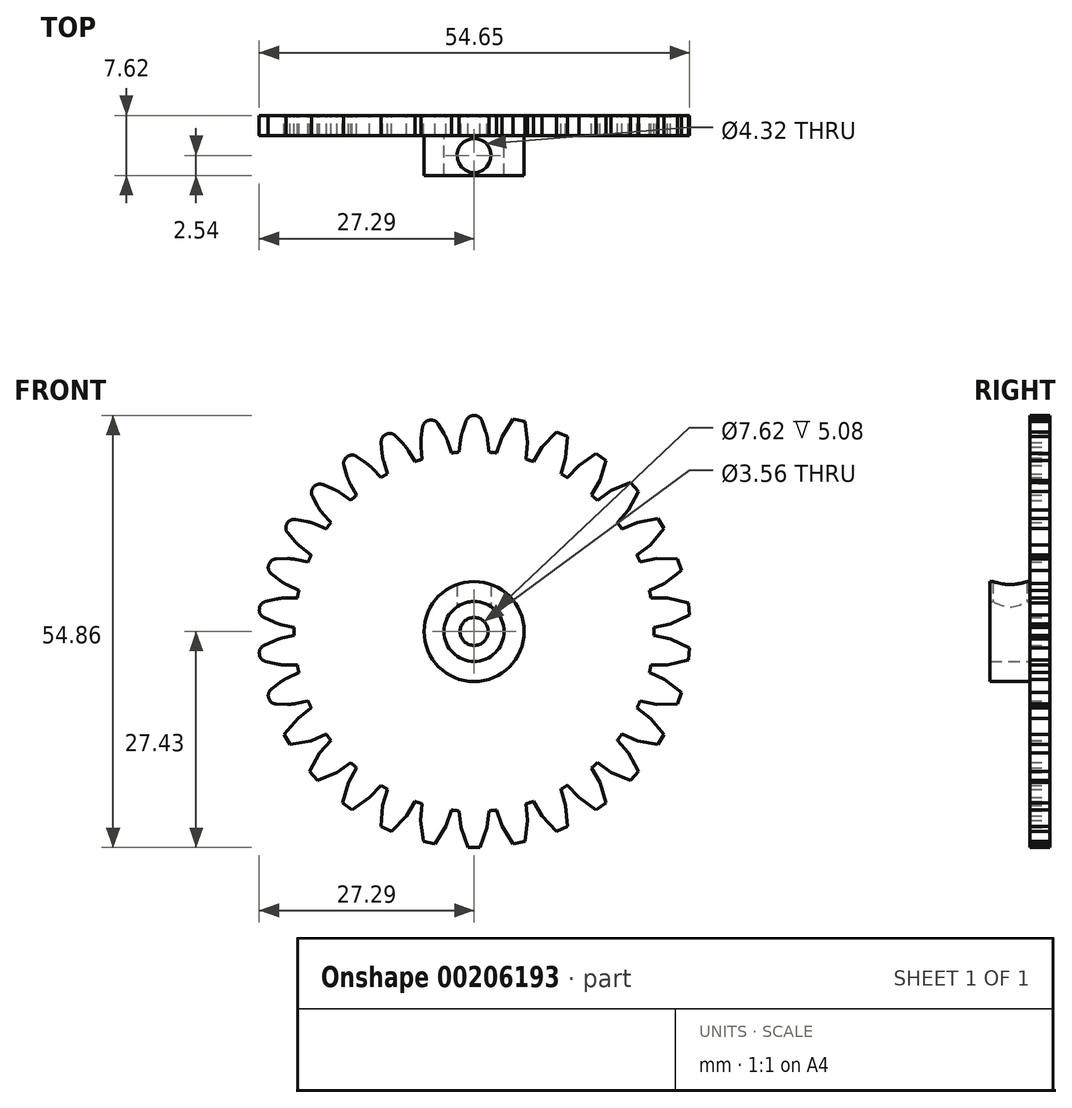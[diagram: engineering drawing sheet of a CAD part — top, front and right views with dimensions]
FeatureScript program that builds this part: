
annotation { "Feature Type Name" : "Feature", "Feature Type Description" : "" }
export const myFeature = defineFeature(function(context is Context, id is Id, definition is map)
    precondition{}
    {
        {
            var Q0;
            Q0=qCreatedBy(makeId("Front.planeOp"),FACE);
            var sketch = newSketch(context, id + "F0", { "sketchPlane" : qUnion([Q0])});
            skCircle(sketch, "E0", {"center": v(0, 0) * mm, "radius": 22.86 * mm});
            skLineSegment(sketch, "E1", {"start": v(-1.9, 22.78) * mm, "end": v(-0.76, 27.43) * mm, "construction": true});
            skLineSegment(sketch, "E2", {"start": v(-0.76, 27.43) * mm, "end": v(0.76, 27.43) * mm});
            skLineSegment(sketch, "E3", {"start": v(0.76, 27.43) * mm, "end": v(1.9, 22.78) * mm, "construction": true});
            skLineSegment(sketch, "E4", {"start": v(-1.9, 22.78) * mm, "end": v(-1.65, 24.9) * mm});
            skPoint(sketch, "E4.endSnap0", {"position": v(-1.33, 25.1) * mm});
            skLineSegment(sketch, "E5", {"start": v(-1.65, 24.9) * mm, "end": v(-0.76, 27.43) * mm});
            skLineSegment(sketch, "E6", {"start": v(1.9, 22.78) * mm, "end": v(1.65, 24.9) * mm});
            skPoint(sketch, "E6.endSnap0", {"position": v(1.33, 25.1) * mm});
            skLineSegment(sketch, "E7", {"start": v(1.65, 24.9) * mm, "end": v(0.76, 27.43) * mm});
            skLineSegment(sketch, "E8.1.0", {"start": v(-6.45, 26.67) * mm, "end": v(-4.96, 27) * mm});
            skLineSegment(sketch, "E8.1.1", {"start": v(-3.56, 24.7) * mm, "end": v(-4.96, 27) * mm});
            skLineSegment(sketch, "E8.1.2", {"start": v(-2.87, 22.68) * mm, "end": v(-3.56, 24.7) * mm});
            skLineSegment(sketch, "E8.1.3", {"start": v(-6.8, 24) * mm, "end": v(-6.45, 26.67) * mm});
            skLineSegment(sketch, "E8.1.4", {"start": v(-6.6, 21.89) * mm, "end": v(-6.8, 24) * mm});
            skLineSegment(sketch, "E8.2.0", {"start": v(-11.85, 24.75) * mm, "end": v(-10.46, 25.37) * mm});
            skLineSegment(sketch, "E8.2.1", {"start": v(-8.62, 23.41) * mm, "end": v(-10.46, 25.37) * mm});
            skLineSegment(sketch, "E8.2.2", {"start": v(-7.53, 21.59) * mm, "end": v(-8.62, 23.41) * mm});
            skLineSegment(sketch, "E8.2.3", {"start": v(-11.63, 22.07) * mm, "end": v(-11.85, 24.75) * mm});
            skLineSegment(sketch, "E8.2.4", {"start": v(-11, 20.04) * mm, "end": v(-11.63, 22.07) * mm});
            skLineSegment(sketch, "E8.3.0", {"start": v(-16.74, 21.75) * mm, "end": v(-15.5, 22.64) * mm});
            skLineSegment(sketch, "E8.3.1", {"start": v(-13.3, 21.1) * mm, "end": v(-15.5, 22.64) * mm});
            skLineSegment(sketch, "E8.3.2", {"start": v(-11.85, 19.55) * mm, "end": v(-13.3, 21.1) * mm});
            skLineSegment(sketch, "E8.3.3", {"start": v(-15.97, 19.17) * mm, "end": v(-16.74, 21.75) * mm});
            skLineSegment(sketch, "E8.3.4", {"start": v(-14.93, 17.31) * mm, "end": v(-15.97, 19.17) * mm});
            skLineSegment(sketch, "E8.4.0", {"start": v(-20.9, 17.79) * mm, "end": v(-19.88, 18.92) * mm});
            skLineSegment(sketch, "E8.4.1", {"start": v(-17.4, 17.88) * mm, "end": v(-19.88, 18.92) * mm});
            skLineSegment(sketch, "E8.4.2", {"start": v(-15.65, 16.66) * mm, "end": v(-17.4, 17.88) * mm});
            skLineSegment(sketch, "E8.4.3", {"start": v(-19.6, 15.43) * mm, "end": v(-20.9, 17.79) * mm});
            skLineSegment(sketch, "E8.4.4", {"start": v(-18.2, 13.83) * mm, "end": v(-19.6, 15.43) * mm});
            skLineSegment(sketch, "E8.5.0", {"start": v(-24.14, 13.06) * mm, "end": v(-23.38, 14.38) * mm});
            skLineSegment(sketch, "E8.5.1", {"start": v(-20.73, 13.88) * mm, "end": v(-23.38, 14.38) * mm});
            skLineSegment(sketch, "E8.5.2", {"start": v(-18.78, 13.04) * mm, "end": v(-20.73, 13.88) * mm});
            skLineSegment(sketch, "E8.5.3", {"start": v(-22.38, 11.02) * mm, "end": v(-24.14, 13.06) * mm});
            skLineSegment(sketch, "E8.5.4", {"start": v(-20.68, 9.74) * mm, "end": v(-22.38, 11.02) * mm});
            skLineSegment(sketch, "E8.6.0", {"start": v(-26.32, 7.75) * mm, "end": v(-25.85, 9.2) * mm});
            skLineSegment(sketch, "E8.6.1", {"start": v(-23.16, 9.26) * mm, "end": v(-25.85, 9.2) * mm});
            skLineSegment(sketch, "E8.6.2", {"start": v(-21.08, 8.85) * mm, "end": v(-23.16, 9.26) * mm});
            skLineSegment(sketch, "E8.6.3", {"start": v(-24.18, 6.12) * mm, "end": v(-26.32, 7.75) * mm});
            skLineSegment(sketch, "E8.6.4", {"start": v(-22.25, 5.23) * mm, "end": v(-24.18, 6.12) * mm});
            skLineSegment(sketch, "E8.7.0", {"start": v(-27.36, 2.1) * mm, "end": v(-27.2, 3.63) * mm});
            skLineSegment(sketch, "E8.7.1", {"start": v(-24.58, 4.24) * mm, "end": v(-27.2, 3.63) * mm});
            skLineSegment(sketch, "E8.7.2", {"start": v(-22.46, 4.28) * mm, "end": v(-24.58, 4.24) * mm});
            skLineSegment(sketch, "E8.7.3", {"start": v(-24.93, 0.96) * mm, "end": v(-27.36, 2.1) * mm});
            skLineSegment(sketch, "E8.7.4", {"start": v(-22.85, 0.49) * mm, "end": v(-24.93, 0.96) * mm});
            skLineSegment(sketch, "E8.8.0", {"start": v(-27.2, -3.63) * mm, "end": v(-27.36, -2.1) * mm});
            skLineSegment(sketch, "E8.8.1", {"start": v(-24.93, -0.96) * mm, "end": v(-27.36, -2.1) * mm});
            skLineSegment(sketch, "E8.8.2", {"start": v(-22.85, -0.49) * mm, "end": v(-24.93, -0.96) * mm});
            skLineSegment(sketch, "E8.8.3", {"start": v(-24.58, -4.24) * mm, "end": v(-27.2, -3.63) * mm});
            skLineSegment(sketch, "E8.8.4", {"start": v(-22.46, -4.28) * mm, "end": v(-24.58, -4.24) * mm});
            skLineSegment(sketch, "E8.9.0", {"start": v(-25.85, -9.2) * mm, "end": v(-26.32, -7.75) * mm});
            skLineSegment(sketch, "E8.9.1", {"start": v(-24.18, -6.12) * mm, "end": v(-26.32, -7.75) * mm});
            skLineSegment(sketch, "E8.9.2", {"start": v(-22.25, -5.23) * mm, "end": v(-24.18, -6.12) * mm});
            skLineSegment(sketch, "E8.9.3", {"start": v(-23.16, -9.26) * mm, "end": v(-25.85, -9.2) * mm});
            skLineSegment(sketch, "E8.9.4", {"start": v(-21.08, -8.85) * mm, "end": v(-23.16, -9.26) * mm});
            skCircle(sketch, "E9", {"center": v(0, 0) * mm, "radius": 1.78 * mm});
            skLineSegment(sketch, "E10.3.10.0", {"start": v(-22.38, -11.02) * mm, "end": v(-24.14, -13.06) * mm});
            skLineSegment(sketch, "E10.6.10.0", {"start": v(-20.68, -9.74) * mm, "end": v(-22.38, -11.02) * mm});
            skLineSegment(sketch, "E10.9.10.0", {"start": v(-20.73, -13.88) * mm, "end": v(-23.38, -14.38) * mm});
            skLineSegment(sketch, "E10.12.10.0", {"start": v(-18.78, -13.04) * mm, "end": v(-20.73, -13.88) * mm});
            skLineSegment(sketch, "E10.13.10.0", {"start": v(-23.38, -14.38) * mm, "end": v(-24.14, -13.06) * mm});
            skLineSegment(sketch, "E10.3.11.0", {"start": v(-19.6, -15.43) * mm, "end": v(-20.9, -17.79) * mm});
            skLineSegment(sketch, "E10.6.11.0", {"start": v(-18.2, -13.83) * mm, "end": v(-19.6, -15.43) * mm});
            skLineSegment(sketch, "E10.9.11.0", {"start": v(-17.4, -17.88) * mm, "end": v(-19.88, -18.92) * mm});
            skLineSegment(sketch, "E10.12.11.0", {"start": v(-15.65, -16.66) * mm, "end": v(-17.4, -17.88) * mm});
            skLineSegment(sketch, "E10.13.11.0", {"start": v(-19.88, -18.92) * mm, "end": v(-20.9, -17.79) * mm});
            skLineSegment(sketch, "E10.3.12.0", {"start": v(-15.97, -19.17) * mm, "end": v(-16.74, -21.75) * mm});
            skLineSegment(sketch, "E10.6.12.0", {"start": v(-14.93, -17.31) * mm, "end": v(-15.97, -19.17) * mm});
            skLineSegment(sketch, "E10.9.12.0", {"start": v(-13.3, -21.1) * mm, "end": v(-15.5, -22.64) * mm});
            skLineSegment(sketch, "E10.12.12.0", {"start": v(-11.85, -19.55) * mm, "end": v(-13.3, -21.1) * mm});
            skLineSegment(sketch, "E10.13.12.0", {"start": v(-15.5, -22.64) * mm, "end": v(-16.74, -21.75) * mm});
            skLineSegment(sketch, "E10.3.13.0", {"start": v(-11.63, -22.07) * mm, "end": v(-11.85, -24.75) * mm});
            skLineSegment(sketch, "E10.6.13.0", {"start": v(-11, -20.04) * mm, "end": v(-11.63, -22.07) * mm});
            skLineSegment(sketch, "E10.9.13.0", {"start": v(-8.62, -23.41) * mm, "end": v(-10.46, -25.37) * mm});
            skLineSegment(sketch, "E10.12.13.0", {"start": v(-7.53, -21.59) * mm, "end": v(-8.62, -23.41) * mm});
            skLineSegment(sketch, "E10.13.13.0", {"start": v(-10.46, -25.37) * mm, "end": v(-11.85, -24.75) * mm});
            skLineSegment(sketch, "E10.3.14.0", {"start": v(-6.8, -24) * mm, "end": v(-6.45, -26.67) * mm});
            skLineSegment(sketch, "E10.6.14.0", {"start": v(-6.6, -21.89) * mm, "end": v(-6.8, -24) * mm});
            skLineSegment(sketch, "E10.9.14.0", {"start": v(-3.56, -24.7) * mm, "end": v(-4.96, -27) * mm});
            skLineSegment(sketch, "E10.12.14.0", {"start": v(-2.87, -22.68) * mm, "end": v(-3.56, -24.7) * mm});
            skLineSegment(sketch, "E10.13.14.0", {"start": v(-4.96, -27) * mm, "end": v(-6.45, -26.67) * mm});
            skLineSegment(sketch, "E10.3.15.0", {"start": v(-1.65, -24.9) * mm, "end": v(-0.76, -27.43) * mm});
            skLineSegment(sketch, "E10.6.15.0", {"start": v(-1.9, -22.78) * mm, "end": v(-1.65, -24.9) * mm});
            skLineSegment(sketch, "E10.9.15.0", {"start": v(1.65, -24.9) * mm, "end": v(0.76, -27.43) * mm});
            skLineSegment(sketch, "E10.12.15.0", {"start": v(1.9, -22.78) * mm, "end": v(1.65, -24.9) * mm});
            skLineSegment(sketch, "E10.13.15.0", {"start": v(0.76, -27.43) * mm, "end": v(-0.76, -27.43) * mm});
            skLineSegment(sketch, "E10.3.16.0", {"start": v(3.56, -24.7) * mm, "end": v(4.96, -27) * mm});
            skLineSegment(sketch, "E10.6.16.0", {"start": v(2.87, -22.68) * mm, "end": v(3.56, -24.7) * mm});
            skLineSegment(sketch, "E10.9.16.0", {"start": v(6.8, -24) * mm, "end": v(6.45, -26.67) * mm});
            skLineSegment(sketch, "E10.12.16.0", {"start": v(6.6, -21.89) * mm, "end": v(6.8, -24) * mm});
            skLineSegment(sketch, "E10.13.16.0", {"start": v(6.45, -26.67) * mm, "end": v(4.96, -27) * mm});
            skLineSegment(sketch, "E10.3.17.0", {"start": v(8.62, -23.41) * mm, "end": v(10.46, -25.37) * mm});
            skLineSegment(sketch, "E10.6.17.0", {"start": v(7.53, -21.59) * mm, "end": v(8.62, -23.41) * mm});
            skLineSegment(sketch, "E10.9.17.0", {"start": v(11.63, -22.07) * mm, "end": v(11.85, -24.75) * mm});
            skLineSegment(sketch, "E10.12.17.0", {"start": v(11, -20.04) * mm, "end": v(11.63, -22.07) * mm});
            skLineSegment(sketch, "E10.13.17.0", {"start": v(11.85, -24.75) * mm, "end": v(10.46, -25.37) * mm});
            skLineSegment(sketch, "E10.3.18.0", {"start": v(13.3, -21.1) * mm, "end": v(15.5, -22.64) * mm});
            skLineSegment(sketch, "E10.6.18.0", {"start": v(11.85, -19.55) * mm, "end": v(13.3, -21.1) * mm});
            skLineSegment(sketch, "E10.9.18.0", {"start": v(15.97, -19.17) * mm, "end": v(16.74, -21.75) * mm});
            skLineSegment(sketch, "E10.12.18.0", {"start": v(14.93, -17.31) * mm, "end": v(15.97, -19.17) * mm});
            skLineSegment(sketch, "E10.13.18.0", {"start": v(16.74, -21.75) * mm, "end": v(15.5, -22.64) * mm});
            skLineSegment(sketch, "E10.3.19.0", {"start": v(17.4, -17.88) * mm, "end": v(19.88, -18.92) * mm});
            skLineSegment(sketch, "E10.6.19.0", {"start": v(15.65, -16.66) * mm, "end": v(17.4, -17.88) * mm});
            skLineSegment(sketch, "E10.9.19.0", {"start": v(19.6, -15.43) * mm, "end": v(20.9, -17.79) * mm});
            skLineSegment(sketch, "E10.12.19.0", {"start": v(18.2, -13.83) * mm, "end": v(19.6, -15.43) * mm});
            skLineSegment(sketch, "E10.13.19.0", {"start": v(20.9, -17.79) * mm, "end": v(19.88, -18.92) * mm});
            skLineSegment(sketch, "E11.3.20.0", {"start": v(20.73, -13.88) * mm, "end": v(23.38, -14.38) * mm});
            skLineSegment(sketch, "E11.6.20.0", {"start": v(18.78, -13.04) * mm, "end": v(20.73, -13.88) * mm});
            skLineSegment(sketch, "E11.9.20.0", {"start": v(22.38, -11.02) * mm, "end": v(24.14, -13.06) * mm});
            skLineSegment(sketch, "E11.12.20.0", {"start": v(20.68, -9.74) * mm, "end": v(22.38, -11.02) * mm});
            skLineSegment(sketch, "E11.13.20.0", {"start": v(24.14, -13.06) * mm, "end": v(23.38, -14.38) * mm});
            skLineSegment(sketch, "E11.3.21.0", {"start": v(23.16, -9.26) * mm, "end": v(25.85, -9.2) * mm});
            skLineSegment(sketch, "E11.6.21.0", {"start": v(21.08, -8.85) * mm, "end": v(23.16, -9.26) * mm});
            skLineSegment(sketch, "E11.9.21.0", {"start": v(24.18, -6.12) * mm, "end": v(26.32, -7.75) * mm});
            skLineSegment(sketch, "E11.12.21.0", {"start": v(22.25, -5.23) * mm, "end": v(24.18, -6.12) * mm});
            skLineSegment(sketch, "E11.13.21.0", {"start": v(26.32, -7.75) * mm, "end": v(25.85, -9.2) * mm});
            skLineSegment(sketch, "E11.3.22.0", {"start": v(24.58, -4.24) * mm, "end": v(27.2, -3.63) * mm});
            skLineSegment(sketch, "E11.6.22.0", {"start": v(22.46, -4.28) * mm, "end": v(24.58, -4.24) * mm});
            skLineSegment(sketch, "E11.9.22.0", {"start": v(24.93, -0.96) * mm, "end": v(27.36, -2.1) * mm});
            skLineSegment(sketch, "E11.12.22.0", {"start": v(22.85, -0.49) * mm, "end": v(24.93, -0.96) * mm});
            skLineSegment(sketch, "E11.13.22.0", {"start": v(27.36, -2.1) * mm, "end": v(27.2, -3.63) * mm});
            skLineSegment(sketch, "E11.3.23.0", {"start": v(24.93, 0.96) * mm, "end": v(27.36, 2.1) * mm});
            skLineSegment(sketch, "E11.6.23.0", {"start": v(22.85, 0.49) * mm, "end": v(24.93, 0.96) * mm});
            skLineSegment(sketch, "E11.9.23.0", {"start": v(24.58, 4.24) * mm, "end": v(27.2, 3.63) * mm});
            skLineSegment(sketch, "E11.12.23.0", {"start": v(22.46, 4.28) * mm, "end": v(24.58, 4.24) * mm});
            skLineSegment(sketch, "E11.13.23.0", {"start": v(27.2, 3.63) * mm, "end": v(27.36, 2.1) * mm});
            skLineSegment(sketch, "E11.3.24.0", {"start": v(24.18, 6.12) * mm, "end": v(26.32, 7.75) * mm});
            skLineSegment(sketch, "E11.6.24.0", {"start": v(22.25, 5.23) * mm, "end": v(24.18, 6.12) * mm});
            skLineSegment(sketch, "E11.9.24.0", {"start": v(23.16, 9.26) * mm, "end": v(25.85, 9.2) * mm});
            skLineSegment(sketch, "E11.12.24.0", {"start": v(21.08, 8.85) * mm, "end": v(23.16, 9.26) * mm});
            skLineSegment(sketch, "E11.13.24.0", {"start": v(25.85, 9.2) * mm, "end": v(26.32, 7.75) * mm});
            skLineSegment(sketch, "E11.3.25.0", {"start": v(22.38, 11.02) * mm, "end": v(24.14, 13.06) * mm});
            skLineSegment(sketch, "E11.6.25.0", {"start": v(20.68, 9.74) * mm, "end": v(22.38, 11.02) * mm});
            skLineSegment(sketch, "E11.9.25.0", {"start": v(20.73, 13.88) * mm, "end": v(23.38, 14.38) * mm});
            skLineSegment(sketch, "E11.12.25.0", {"start": v(18.78, 13.04) * mm, "end": v(20.73, 13.88) * mm});
            skLineSegment(sketch, "E11.13.25.0", {"start": v(23.38, 14.38) * mm, "end": v(24.14, 13.06) * mm});
            skLineSegment(sketch, "E11.3.26.0", {"start": v(19.6, 15.43) * mm, "end": v(20.9, 17.79) * mm});
            skLineSegment(sketch, "E11.6.26.0", {"start": v(18.2, 13.83) * mm, "end": v(19.6, 15.43) * mm});
            skLineSegment(sketch, "E11.9.26.0", {"start": v(17.4, 17.88) * mm, "end": v(19.88, 18.92) * mm});
            skLineSegment(sketch, "E11.12.26.0", {"start": v(15.65, 16.66) * mm, "end": v(17.4, 17.88) * mm});
            skLineSegment(sketch, "E11.13.26.0", {"start": v(19.88, 18.92) * mm, "end": v(20.9, 17.79) * mm});
            skLineSegment(sketch, "E11.3.27.0", {"start": v(15.97, 19.17) * mm, "end": v(16.74, 21.75) * mm});
            skLineSegment(sketch, "E11.6.27.0", {"start": v(14.93, 17.31) * mm, "end": v(15.97, 19.17) * mm});
            skLineSegment(sketch, "E11.9.27.0", {"start": v(13.3, 21.1) * mm, "end": v(15.5, 22.64) * mm});
            skLineSegment(sketch, "E11.12.27.0", {"start": v(11.85, 19.55) * mm, "end": v(13.3, 21.1) * mm});
            skLineSegment(sketch, "E11.13.27.0", {"start": v(15.5, 22.64) * mm, "end": v(16.74, 21.75) * mm});
            skLineSegment(sketch, "E11.3.28.0", {"start": v(11.63, 22.07) * mm, "end": v(11.85, 24.75) * mm});
            skLineSegment(sketch, "E11.6.28.0", {"start": v(11, 20.04) * mm, "end": v(11.63, 22.07) * mm});
            skLineSegment(sketch, "E11.9.28.0", {"start": v(8.62, 23.41) * mm, "end": v(10.46, 25.37) * mm});
            skLineSegment(sketch, "E11.12.28.0", {"start": v(7.53, 21.59) * mm, "end": v(8.62, 23.41) * mm});
            skLineSegment(sketch, "E11.13.28.0", {"start": v(10.46, 25.37) * mm, "end": v(11.85, 24.75) * mm});
            skLineSegment(sketch, "E11.3.29.0", {"start": v(6.8, 24) * mm, "end": v(6.45, 26.67) * mm});
            skLineSegment(sketch, "E11.6.29.0", {"start": v(6.6, 21.89) * mm, "end": v(6.8, 24) * mm});
            skLineSegment(sketch, "E11.9.29.0", {"start": v(3.56, 24.7) * mm, "end": v(4.96, 27) * mm});
            skLineSegment(sketch, "E11.12.29.0", {"start": v(2.87, 22.68) * mm, "end": v(3.56, 24.7) * mm});
            skLineSegment(sketch, "E11.13.29.0", {"start": v(4.96, 27) * mm, "end": v(6.45, 26.67) * mm});
            skSolve(sketch);
        }
        {
            var Q0;
            Q0=qSketchRegion(id+"F0",true);
            extrude(context, id + "F1", {"entities" : qUnion([Q0]), "depth" : 2.54 * mm});
        }
        {
            var Q0;
            Q0=makeQuery(id+"F1.opExtrude","CAP_FACE",FACE,{"disambiguationData":[OSD([sQuery(id+"F0.wireOp",EDGE,"E0"),sQuery(id+"F0.wireOp",EDGE,"E2"),sQuery(id+"F0.wireOp",EDGE,"E4"),sQuery(id+"F0.wireOp",EDGE,"E5"),sQuery(id+"F0.wireOp",EDGE,"E6"),sQuery(id+"F0.wireOp",EDGE,"E7"),sQuery(id+"F0.wireOp",EDGE,"E8.1.0"),sQuery(id+"F0.wireOp",EDGE,"E8.1.1"),sQuery(id+"F0.wireOp",EDGE,"E8.1.2"),sQuery(id+"F0.wireOp",EDGE,"E8.1.3"),sQuery(id+"F0.wireOp",EDGE,"E8.1.4"),sQuery(id+"F0.wireOp",EDGE,"E8.2.0"),sQuery(id+"F0.wireOp",EDGE,"E8.2.1"),sQuery(id+"F0.wireOp",EDGE,"E8.2.2"),sQuery(id+"F0.wireOp",EDGE,"E8.2.3"),sQuery(id+"F0.wireOp",EDGE,"E8.2.4"),sQuery(id+"F0.wireOp",EDGE,"E8.3.0"),sQuery(id+"F0.wireOp",EDGE,"E8.3.1"),sQuery(id+"F0.wireOp",EDGE,"E8.3.2"),sQuery(id+"F0.wireOp",EDGE,"E8.3.3"),sQuery(id+"F0.wireOp",EDGE,"E8.3.4"),sQuery(id+"F0.wireOp",EDGE,"E8.4.0"),sQuery(id+"F0.wireOp",EDGE,"E8.4.1"),sQuery(id+"F0.wireOp",EDGE,"E8.4.2"),sQuery(id+"F0.wireOp",EDGE,"E8.4.3"),sQuery(id+"F0.wireOp",EDGE,"E8.4.4"),sQuery(id+"F0.wireOp",EDGE,"E8.5.0"),sQuery(id+"F0.wireOp",EDGE,"E8.5.1"),sQuery(id+"F0.wireOp",EDGE,"E8.5.2"),sQuery(id+"F0.wireOp",EDGE,"E8.5.3"),sQuery(id+"F0.wireOp",EDGE,"E8.5.4"),sQuery(id+"F0.wireOp",EDGE,"E8.6.0"),sQuery(id+"F0.wireOp",EDGE,"E8.6.1"),sQuery(id+"F0.wireOp",EDGE,"E8.6.2"),sQuery(id+"F0.wireOp",EDGE,"E8.6.3"),sQuery(id+"F0.wireOp",EDGE,"E8.6.4"),sQuery(id+"F0.wireOp",EDGE,"E8.7.0"),sQuery(id+"F0.wireOp",EDGE,"E8.7.1"),sQuery(id+"F0.wireOp",EDGE,"E8.7.2"),sQuery(id+"F0.wireOp",EDGE,"E8.7.3"),sQuery(id+"F0.wireOp",EDGE,"E8.7.4"),sQuery(id+"F0.wireOp",EDGE,"E8.8.0"),sQuery(id+"F0.wireOp",EDGE,"E8.8.1"),sQuery(id+"F0.wireOp",EDGE,"E8.8.2"),sQuery(id+"F0.wireOp",EDGE,"E8.8.3"),sQuery(id+"F0.wireOp",EDGE,"E8.8.4"),sQuery(id+"F0.wireOp",EDGE,"E8.9.0"),sQuery(id+"F0.wireOp",EDGE,"E8.9.1"),sQuery(id+"F0.wireOp",EDGE,"E8.9.2"),sQuery(id+"F0.wireOp",EDGE,"E8.9.3"),sQuery(id+"F0.wireOp",EDGE,"E8.9.4"),sQuery(id+"F0.wireOp",EDGE,"E9")])],"isStart":false});
            var sketch = newSketch(context, id + "F2", { "sketchPlane" : qUnion([Q0])});
            skCircle(sketch, "E12", {"center": v(0, 0) * mm, "radius": 6.35 * mm});
            skCircle(sketch, "E13", {"center": v(0, 0) * mm, "radius": 3.81 * mm});
            skSolve(sketch);
        }
        {
            var Q0;
            Q0=qSketchRegion(id+"F2",true);
            extrude(context, id + "F3", {"entities" : qUnion([Q0]), "operationType" : NewBodyOperationType.ADD, "depth" : 5.08 * mm});
        }
        {
            var Q0;
            Q0=makeQuery(id+"F1.opExtrude","SWEPT_EDGE",EDGE,{"disambiguationData":[OSD([sQuery(id+"F0.wireOp",EDGE,"E8.9.1"),sQuery(id+"F0.wireOp",EDGE,"E8.9.2")])]});
            var Q1;
            Q1=makeQuery(id+"F1.opExtrude","SWEPT_EDGE",EDGE,{"disambiguationData":[OSD([sQuery(id+"F0.wireOp",EDGE,"E8.9.3"),sQuery(id+"F0.wireOp",EDGE,"E8.9.4")])]});
            var Q2;
            Q2=makeQuery(id+"F1.opExtrude","SWEPT_EDGE",EDGE,{"disambiguationData":[OSD([sQuery(id+"F0.wireOp",EDGE,"E6"),sQuery(id+"F0.wireOp",EDGE,"E7")])]});
            var Q3;
            Q3=makeQuery(id+"F1.opExtrude","SWEPT_EDGE",EDGE,{"disambiguationData":[OSD([sQuery(id+"F0.wireOp",EDGE,"E8.1.1"),sQuery(id+"F0.wireOp",EDGE,"E8.1.2")])]});
            var Q4;
            Q4=makeQuery(id+"F1.opExtrude","SWEPT_EDGE",EDGE,{"disambiguationData":[OSD([sQuery(id+"F0.wireOp",EDGE,"E8.2.1"),sQuery(id+"F0.wireOp",EDGE,"E8.2.2")])]});
            var Q5;
            Q5=makeQuery(id+"F1.opExtrude","SWEPT_EDGE",EDGE,{"disambiguationData":[OSD([sQuery(id+"F0.wireOp",EDGE,"E8.3.1"),sQuery(id+"F0.wireOp",EDGE,"E8.3.2")])]});
            var Q6;
            Q6=makeQuery(id+"F1.opExtrude","SWEPT_EDGE",EDGE,{"disambiguationData":[OSD([sQuery(id+"F0.wireOp",EDGE,"E8.4.1"),sQuery(id+"F0.wireOp",EDGE,"E8.4.2")])]});
            var Q7;
            Q7=makeQuery(id+"F1.opExtrude","SWEPT_EDGE",EDGE,{"disambiguationData":[OSD([sQuery(id+"F0.wireOp",EDGE,"E8.5.1"),sQuery(id+"F0.wireOp",EDGE,"E8.5.2")])]});
            var Q8;
            Q8=makeQuery(id+"F1.opExtrude","SWEPT_EDGE",EDGE,{"disambiguationData":[OSD([sQuery(id+"F0.wireOp",EDGE,"E8.6.1"),sQuery(id+"F0.wireOp",EDGE,"E8.6.2")])]});
            var Q9;
            Q9=makeQuery(id+"F1.opExtrude","SWEPT_EDGE",EDGE,{"disambiguationData":[OSD([sQuery(id+"F0.wireOp",EDGE,"E8.7.1"),sQuery(id+"F0.wireOp",EDGE,"E8.7.2")])]});
            var Q10;
            Q10=makeQuery(id+"F1.opExtrude","SWEPT_EDGE",EDGE,{"disambiguationData":[OSD([sQuery(id+"F0.wireOp",EDGE,"E8.8.1"),sQuery(id+"F0.wireOp",EDGE,"E8.8.2")])]});
            var Q11;
            Q11=makeQuery(id+"F1.opExtrude","SWEPT_EDGE",EDGE,{"disambiguationData":[OSD([sQuery(id+"F0.wireOp",EDGE,"E8.7.3"),sQuery(id+"F0.wireOp",EDGE,"E8.7.4")])]});
            var Q12;
            Q12=makeQuery(id+"F1.opExtrude","SWEPT_EDGE",EDGE,{"disambiguationData":[OSD([sQuery(id+"F0.wireOp",EDGE,"E8.8.3"),sQuery(id+"F0.wireOp",EDGE,"E8.8.4")])]});
            var Q13;
            Q13=makeQuery(id+"F1.opExtrude","SWEPT_EDGE",EDGE,{"disambiguationData":[OSD([sQuery(id+"F0.wireOp",EDGE,"E4"),sQuery(id+"F0.wireOp",EDGE,"E5")])]});
            var Q14;
            Q14=makeQuery(id+"F1.opExtrude","SWEPT_EDGE",EDGE,{"disambiguationData":[OSD([sQuery(id+"F0.wireOp",EDGE,"E8.1.3"),sQuery(id+"F0.wireOp",EDGE,"E8.1.4")])]});
            var Q15;
            Q15=makeQuery(id+"F1.opExtrude","SWEPT_EDGE",EDGE,{"disambiguationData":[OSD([sQuery(id+"F0.wireOp",EDGE,"E8.2.3"),sQuery(id+"F0.wireOp",EDGE,"E8.2.4")])]});
            var Q16;
            Q16=makeQuery(id+"F1.opExtrude","SWEPT_EDGE",EDGE,{"disambiguationData":[OSD([sQuery(id+"F0.wireOp",EDGE,"E8.3.3"),sQuery(id+"F0.wireOp",EDGE,"E8.3.4")])]});
            var Q17;
            Q17=makeQuery(id+"F1.opExtrude","SWEPT_EDGE",EDGE,{"disambiguationData":[OSD([sQuery(id+"F0.wireOp",EDGE,"E8.4.3"),sQuery(id+"F0.wireOp",EDGE,"E8.4.4")])]});
            var Q18;
            Q18=makeQuery(id+"F1.opExtrude","SWEPT_EDGE",EDGE,{"disambiguationData":[OSD([sQuery(id+"F0.wireOp",EDGE,"E8.5.3"),sQuery(id+"F0.wireOp",EDGE,"E8.5.4")])]});
            var Q19;
            Q19=makeQuery(id+"F1.opExtrude","SWEPT_EDGE",EDGE,{"disambiguationData":[OSD([sQuery(id+"F0.wireOp",EDGE,"E8.6.3"),sQuery(id+"F0.wireOp",EDGE,"E8.6.4")])]});
            fillet(context, id + "F4", {"entities" : qUnion([Q0, Q1, Q2, Q3, Q4, Q5, Q6, Q7, Q8, Q9, Q10, Q11, Q12, Q13, Q14, Q15, Q16, Q17, Q18, Q19]), "radius" : 5.08 * mm, "tangentPropagation" : true, "allowEdgeOverflow" : false});
        }
        {
            var Q0;
            Q0=makeQuery(id+"F1.opExtrude","SWEPT_EDGE",EDGE,{"disambiguationData":[OSD([sQuery(id+"F0.wireOp",EDGE,"E2"),sQuery(id+"F0.wireOp",EDGE,"E7")])]});
            var Q1;
            Q1=makeQuery(id+"F1.opExtrude","SWEPT_EDGE",EDGE,{"disambiguationData":[OSD([sQuery(id+"F0.wireOp",EDGE,"E2"),sQuery(id+"F0.wireOp",EDGE,"E5")])]});
            var Q2;
            Q2=makeQuery(id+"F1.opExtrude","SWEPT_EDGE",EDGE,{"disambiguationData":[OSD([sQuery(id+"F0.wireOp",EDGE,"E8.1.0"),sQuery(id+"F0.wireOp",EDGE,"E8.1.1")])]});
            var Q3;
            Q3=makeQuery(id+"F1.opExtrude","SWEPT_EDGE",EDGE,{"disambiguationData":[OSD([sQuery(id+"F0.wireOp",EDGE,"E8.1.0"),sQuery(id+"F0.wireOp",EDGE,"E8.1.3")])]});
            var Q4;
            Q4=makeQuery(id+"F1.opExtrude","SWEPT_EDGE",EDGE,{"disambiguationData":[OSD([sQuery(id+"F0.wireOp",EDGE,"E8.2.0"),sQuery(id+"F0.wireOp",EDGE,"E8.2.1")])]});
            var Q5;
            Q5=makeQuery(id+"F1.opExtrude","SWEPT_EDGE",EDGE,{"disambiguationData":[OSD([sQuery(id+"F0.wireOp",EDGE,"E8.9.0"),sQuery(id+"F0.wireOp",EDGE,"E8.9.3")])]});
            var Q6;
            Q6=makeQuery(id+"F1.opExtrude","SWEPT_EDGE",EDGE,{"disambiguationData":[OSD([sQuery(id+"F0.wireOp",EDGE,"E8.9.0"),sQuery(id+"F0.wireOp",EDGE,"E8.9.1")])]});
            var Q7;
            Q7=makeQuery(id+"F1.opExtrude","SWEPT_EDGE",EDGE,{"disambiguationData":[OSD([sQuery(id+"F0.wireOp",EDGE,"E8.8.0"),sQuery(id+"F0.wireOp",EDGE,"E8.8.3")])]});
            var Q8;
            Q8=makeQuery(id+"F1.opExtrude","SWEPT_EDGE",EDGE,{"disambiguationData":[OSD([sQuery(id+"F0.wireOp",EDGE,"E8.2.0"),sQuery(id+"F0.wireOp",EDGE,"E8.2.3")])]});
            var Q9;
            Q9=makeQuery(id+"F1.opExtrude","SWEPT_EDGE",EDGE,{"disambiguationData":[OSD([sQuery(id+"F0.wireOp",EDGE,"E8.3.0"),sQuery(id+"F0.wireOp",EDGE,"E8.3.1")])]});
            var Q10;
            Q10=makeQuery(id+"F1.opExtrude","SWEPT_EDGE",EDGE,{"disambiguationData":[OSD([sQuery(id+"F0.wireOp",EDGE,"E8.3.0"),sQuery(id+"F0.wireOp",EDGE,"E8.3.3")])]});
            var Q11;
            Q11=makeQuery(id+"F1.opExtrude","SWEPT_EDGE",EDGE,{"disambiguationData":[OSD([sQuery(id+"F0.wireOp",EDGE,"E8.4.0"),sQuery(id+"F0.wireOp",EDGE,"E8.4.1")])]});
            var Q12;
            Q12=makeQuery(id+"F1.opExtrude","SWEPT_EDGE",EDGE,{"disambiguationData":[OSD([sQuery(id+"F0.wireOp",EDGE,"E8.4.0"),sQuery(id+"F0.wireOp",EDGE,"E8.4.3")])]});
            var Q13;
            Q13=makeQuery(id+"F1.opExtrude","SWEPT_EDGE",EDGE,{"disambiguationData":[OSD([sQuery(id+"F0.wireOp",EDGE,"E8.5.0"),sQuery(id+"F0.wireOp",EDGE,"E8.5.1")])]});
            var Q14;
            Q14=makeQuery(id+"F1.opExtrude","SWEPT_EDGE",EDGE,{"disambiguationData":[OSD([sQuery(id+"F0.wireOp",EDGE,"E8.5.0"),sQuery(id+"F0.wireOp",EDGE,"E8.5.3")])]});
            var Q15;
            Q15=makeQuery(id+"F1.opExtrude","SWEPT_EDGE",EDGE,{"disambiguationData":[OSD([sQuery(id+"F0.wireOp",EDGE,"E8.6.0"),sQuery(id+"F0.wireOp",EDGE,"E8.6.1")])]});
            var Q16;
            Q16=makeQuery(id+"F1.opExtrude","SWEPT_EDGE",EDGE,{"disambiguationData":[OSD([sQuery(id+"F0.wireOp",EDGE,"E8.6.0"),sQuery(id+"F0.wireOp",EDGE,"E8.6.3")])]});
            var Q17;
            Q17=makeQuery(id+"F1.opExtrude","SWEPT_EDGE",EDGE,{"disambiguationData":[OSD([sQuery(id+"F0.wireOp",EDGE,"E8.7.0"),sQuery(id+"F0.wireOp",EDGE,"E8.7.3")])]});
            var Q18;
            Q18=makeQuery(id+"F1.opExtrude","SWEPT_EDGE",EDGE,{"disambiguationData":[OSD([sQuery(id+"F0.wireOp",EDGE,"E8.7.0"),sQuery(id+"F0.wireOp",EDGE,"E8.7.1")])]});
            var Q19;
            Q19=makeQuery(id+"F1.opExtrude","SWEPT_EDGE",EDGE,{"disambiguationData":[OSD([sQuery(id+"F0.wireOp",EDGE,"E8.8.0"),sQuery(id+"F0.wireOp",EDGE,"E8.8.1")])]});
            fillet(context, id + "F5", {"entities" : qUnion([Q0, Q1, Q2, Q3, Q4, Q5, Q6, Q7, Q8, Q9, Q10, Q11, Q12, Q13, Q14, Q15, Q16, Q17, Q18, Q19]), "radius" : 1.02 * mm, "tangentPropagation" : true, "allowEdgeOverflow" : false});
        }
        {
            var Q0;
            Q0=qCreatedBy(makeId("Top.planeOp"),FACE);
            var sketch = newSketch(context, id + "F6", { "sketchPlane" : qUnion([Q0])});
            skCircle(sketch, "E14", {"center": v(0, -5.08) * mm, "radius": 2.16 * mm});
            skSolve(sketch);
        }
        {
            var Q0;
            Q0=qSketchRegion(id+"F6",true);
            extrude(context, id + "F7", {"entities" : qUnion([Q0]), "operationType" : NewBodyOperationType.REMOVE, "depth" : 25.4 * mm});
        }
    });
